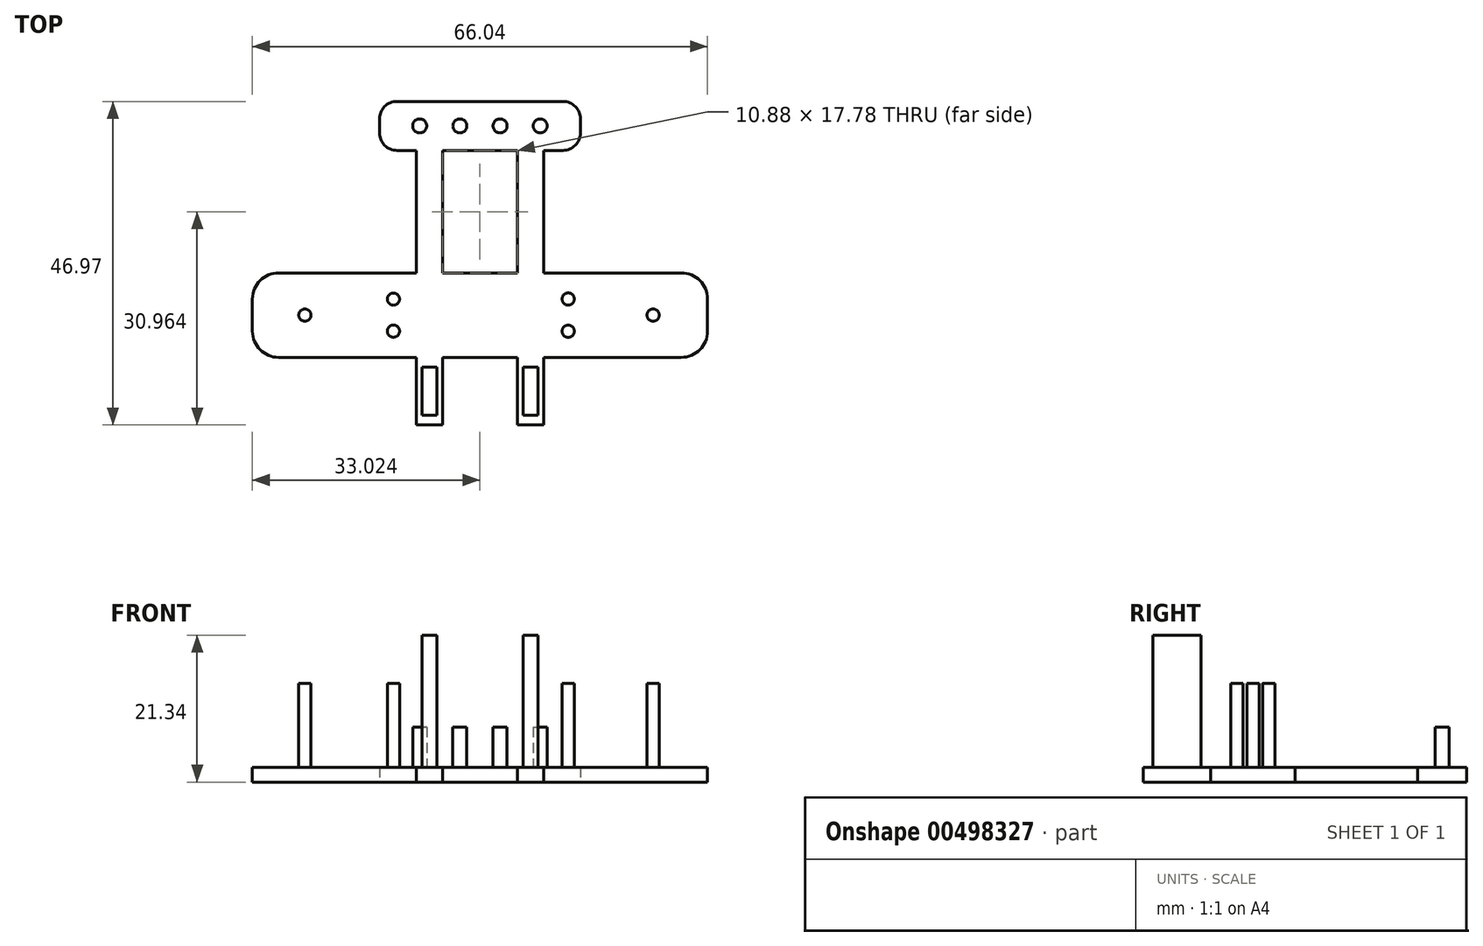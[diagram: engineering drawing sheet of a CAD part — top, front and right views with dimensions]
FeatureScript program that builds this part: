
annotation { "Feature Type Name" : "Feature", "Feature Type Description" : "" }
export const myFeature = defineFeature(function(context is Context, id is Id, definition is map)
    precondition{}
    {
        {
            var Q0;
            Q0=qCreatedBy(makeId("Top.planeOp"),FACE);
            var sketch = newSketch(context, id + "F0", { "sketchPlane" : qUnion([Q0])});
            skLineSegment(sketch, "E0.bottom", {"start": v(33.02, -6.13) * mm, "end": v(-33.02, -6.13) * mm});
            skLineSegment(sketch, "E0.top", {"start": v(29.21, 6.13) * mm, "end": v(-29.21, 6.13) * mm});
            skLineSegment(sketch, "E0.left", {"start": v(33.02, -2.32) * mm, "end": v(33.02, 2.32) * mm});
            skLineSegment(sketch, "E0.right", {"start": v(-33.02, -2.32) * mm, "end": v(-33.02, 2.32) * mm});
            skPoint(sketch, "E0.middle", {"position": v(0, 0) * mm});
            skLineSegment(sketch, "E1", {"start": v(-29.21, -6.13) * mm, "end": v(-9.25, -6.13) * mm});
            skLineSegment(sketch, "E2", {"start": v(29.21, -6.13) * mm, "end": v(9.25, -6.13) * mm});
            skLineSegment(sketch, "E3", {"start": v(9.25, -6.13) * mm, "end": v(9.25, -15.94) * mm});
            skLineSegment(sketch, "E4", {"start": v(9.25, -15.94) * mm, "end": v(5.44, -15.94) * mm});
            skLineSegment(sketch, "E5", {"start": v(5.44, -15.94) * mm, "end": v(5.44, -6.13) * mm});
            skLineSegment(sketch, "E6", {"start": v(-9.25, -6.13) * mm, "end": v(-9.25, -15.94) * mm});
            skLineSegment(sketch, "E7", {"start": v(-9.25, -15.94) * mm, "end": v(-5.44, -15.94) * mm});
            skLineSegment(sketch, "E8", {"start": v(-5.44, -15.94) * mm, "end": v(-5.44, -6.13) * mm});
            skLineSegment(sketch, "E9", {"start": v(-9.25, 6.13) * mm, "end": v(-9.25, 23.91) * mm});
            skLineSegment(sketch, "E10", {"start": v(-9.25, 23.91) * mm, "end": v(-5.44, 23.91) * mm});
            skLineSegment(sketch, "E11", {"start": v(-5.44, 23.91) * mm, "end": v(-5.44, 6.13) * mm});
            skPoint(sketch, "E12.endSnap0", {"position": v(-9.25, 15.02) * mm});
            skLineSegment(sketch, "E13", {"start": v(5.44, 6.13) * mm, "end": v(5.44, 23.91) * mm});
            skLineSegment(sketch, "E14", {"start": v(5.44, 23.91) * mm, "end": v(9.25, 23.91) * mm});
            skLineSegment(sketch, "E15", {"start": v(9.25, 23.91) * mm, "end": v(9.25, 6.13) * mm});
            skPoint(sketch, "E16.startSnap0", {"position": v(0, 6.13) * mm});
            skLineSegment(sketch, "E17", {"start": v(0, 23.91) * mm, "end": v(0, 27.47) * mm});
            skLineSegment(sketch, "E18.bottom", {"start": v(12.04, 23.91) * mm, "end": v(-12.04, 23.91) * mm});
            skLineSegment(sketch, "E18.top", {"start": v(12.04, 31.03) * mm, "end": v(-12.04, 31.03) * mm});
            skLineSegment(sketch, "E18.left", {"start": v(14.58, 26.45) * mm, "end": v(14.58, 28.49) * mm});
            skLineSegment(sketch, "E18.right", {"start": v(-14.58, 26.45) * mm, "end": v(-14.58, 28.49) * mm});
            skPoint(sketch, "E18.middle", {"position": v(0, 27.47) * mm});
            skPoint(sketch, "E19.visualSharp", {"position": v(-33.02, 6.13) * mm});
            skArc(sketch, "E19.filletArc", {"start": v(-29.21, 6.13) * mm, "mid": v(-31.9, 5.02) * mm, "end": v(-33.02, 2.32) * mm});
            skPoint(sketch, "E20.visualSharp", {"position": v(33.02, 6.13) * mm});
            skArc(sketch, "E20.filletArc", {"start": v(33.02, 2.32) * mm, "mid": v(31.9, 5.02) * mm, "end": v(29.21, 6.13) * mm});
            skPoint(sketch, "E21.visualSharp", {"position": v(-14.58, 31.03) * mm});
            skArc(sketch, "E21.filletArc", {"start": v(-12.04, 31.03) * mm, "mid": v(-13.84, 30.28) * mm, "end": v(-14.58, 28.49) * mm});
            skPoint(sketch, "E22.visualSharp", {"position": v(-14.58, 23.91) * mm});
            skArc(sketch, "E22.filletArc", {"start": v(-14.58, 26.45) * mm, "mid": v(-13.84, 24.66) * mm, "end": v(-12.04, 23.91) * mm});
            skPoint(sketch, "E23.visualSharp", {"position": v(14.58, 31.03) * mm});
            skArc(sketch, "E23.filletArc", {"start": v(14.58, 28.49) * mm, "mid": v(13.84, 30.28) * mm, "end": v(12.04, 31.03) * mm});
            skPoint(sketch, "E24.visualSharp", {"position": v(14.58, 23.91) * mm});
            skArc(sketch, "E24.filletArc", {"start": v(12.04, 23.91) * mm, "mid": v(13.84, 24.66) * mm, "end": v(14.58, 26.45) * mm});
            skPoint(sketch, "E25.visualSharp", {"position": v(-33.02, -6.13) * mm});
            skArc(sketch, "E25.filletArc", {"start": v(-33.02, -2.32) * mm, "mid": v(-31.9, -5.02) * mm, "end": v(-29.21, -6.13) * mm});
            skPoint(sketch, "E26.visualSharp", {"position": v(33.02, -6.13) * mm});
            skArc(sketch, "E26.filletArc", {"start": v(29.21, -6.13) * mm, "mid": v(31.9, -5.02) * mm, "end": v(33.02, -2.32) * mm});
            skSolve(sketch);
        }
        {
            var Q0;
            Q0=makeQuery(id+"F0.imprint","IMPRINT",FACE,{"disambiguationData":[TD([[makeQuery(id+"F0.imprint","IMPRINT",EDGE,{"derivedFrom":sQuery(id+"F0.wireOp",EDGE,"E0.left")}),1.0]])]});
            var Q1;
            {var subQ0=sQuery(id+"F0.wireOp",EDGE,"E9");Q1=makeQuery(id+"F0.imprint","IMPRINT",FACE,{"disambiguationData":[TD([[makeQuery(id+"F0.imprint","IMPRINT",EDGE,{"derivedFrom":subQ0}),-1.0]])]});}
            var Q2;
            Q2=makeQuery(id+"F0.imprint","IMPRINT",FACE,{"disambiguationData":[TD([[makeQuery(id+"F0.imprint","IMPRINT",EDGE,{"derivedFrom":sQuery(id+"F0.wireOp",EDGE,"E18.top")}),1.0]])]});
            var Q3;
            {var subQ0=sQuery(id+"F0.wireOp",EDGE,"E13");Q3=makeQuery(id+"F0.imprint","IMPRINT",FACE,{"disambiguationData":[TD([[makeQuery(id+"F0.imprint","IMPRINT",EDGE,{"derivedFrom":subQ0}),-1.0]])]});}
            var Q4;
            {var subQ0=sQuery(id+"F0.wireOp",EDGE,"E3");Q4=makeQuery(id+"F0.imprint","IMPRINT",FACE,{"disambiguationData":[TD([[makeQuery(id+"F0.imprint","IMPRINT",EDGE,{"derivedFrom":subQ0}),-1.0]])]});}
            var Q5;
            {var subQ0=sQuery(id+"F0.wireOp",EDGE,"E6");Q5=makeQuery(id+"F0.imprint","IMPRINT",FACE,{"disambiguationData":[TD([[makeQuery(id+"F0.imprint","IMPRINT",EDGE,{"derivedFrom":subQ0}),1.0]])]});}
            extrude(context, id + "F1", {"entities" : qUnion([Q0, Q1, Q2, Q3, Q4, Q5]), "depth" : 2.16 * mm});
        }
        {
            var Q0;
            Q0=makeQuery(id+"F1.opExtrude","CAP_FACE",FACE,{"disambiguationData":[OSD([sQuery(id+"F0.wireOp",EDGE,"E0.bottom"),sQuery(id+"F0.wireOp",EDGE,"E0.top"),sQuery(id+"F0.wireOp",EDGE,"E0.left"),sQuery(id+"F0.wireOp",EDGE,"E0.right"),sQuery(id+"F0.wireOp",EDGE,"E1"),sQuery(id+"F0.wireOp",EDGE,"E2"),sQuery(id+"F0.wireOp",EDGE,"E3"),sQuery(id+"F0.wireOp",EDGE,"E4"),sQuery(id+"F0.wireOp",EDGE,"E5"),sQuery(id+"F0.wireOp",EDGE,"E6"),sQuery(id+"F0.wireOp",EDGE,"E7"),sQuery(id+"F0.wireOp",EDGE,"E8"),sQuery(id+"F0.wireOp",EDGE,"E9"),sQuery(id+"F0.wireOp",EDGE,"E11"),sQuery(id+"F0.wireOp",EDGE,"E13"),sQuery(id+"F0.wireOp",EDGE,"E15"),sQuery(id+"F0.wireOp",EDGE,"E18.bottom"),sQuery(id+"F0.wireOp",EDGE,"E18.top"),sQuery(id+"F0.wireOp",EDGE,"E18.left"),sQuery(id+"F0.wireOp",EDGE,"E18.right"),sQuery(id+"F0.wireOp",EDGE,"E19.filletArc"),sQuery(id+"F0.wireOp",EDGE,"E20.filletArc"),sQuery(id+"F0.wireOp",EDGE,"E21.filletArc"),sQuery(id+"F0.wireOp",EDGE,"E22.filletArc"),sQuery(id+"F0.wireOp",EDGE,"E23.filletArc"),sQuery(id+"F0.wireOp",EDGE,"E24.filletArc"),sQuery(id+"F0.wireOp",EDGE,"E25.filletArc"),sQuery(id+"F0.wireOp",EDGE,"E26.filletArc")])],"isStart":false});
            var sketch = newSketch(context, id + "F2", { "sketchPlane" : qUnion([Q0])});
            skPoint(sketch, "E27.endSnap0", {"position": v(33.02, 0) * mm});
            skCircle(sketch, "E28", {"center": v(-25.4, 0) * mm, "radius": 0.89 * mm});
            skCircle(sketch, "E29", {"center": v(-12.56, 2.32) * mm, "radius": 0.89 * mm});
            skCircle(sketch, "E30", {"center": v(-12.56, -2.32) * mm, "radius": 0.89 * mm});
            skCircle(sketch, "E31", {"center": v(12.8, -2.34) * mm, "radius": 0.89 * mm});
            skCircle(sketch, "E32", {"center": v(12.8, 2.34) * mm, "radius": 0.89 * mm});
            skCircle(sketch, "E33", {"center": v(25.13, 0) * mm, "radius": 0.89 * mm});
            skSolve(sketch);
        }
        {
            var Q0;
            Q0=makeQuery(id+"F2.imprint","IMPRINT",FACE,{"disambiguationData":[TD([[makeQuery(id+"F2.imprint","IMPRINT",EDGE,{"derivedFrom":sQuery(id+"F2.wireOp",EDGE,"E28")}),1.0]])]});
            var Q1;
            Q1=makeQuery(id+"F2.imprint","IMPRINT",FACE,{"disambiguationData":[TD([[makeQuery(id+"F2.imprint","IMPRINT",EDGE,{"derivedFrom":sQuery(id+"F2.wireOp",EDGE,"E30")}),1.0]])]});
            var Q2;
            Q2=makeQuery(id+"F2.imprint","IMPRINT",FACE,{"disambiguationData":[TD([[makeQuery(id+"F2.imprint","IMPRINT",EDGE,{"derivedFrom":sQuery(id+"F2.wireOp",EDGE,"E29")}),1.0]])]});
            var Q3;
            Q3=makeQuery(id+"F2.imprint","IMPRINT",FACE,{"disambiguationData":[TD([[makeQuery(id+"F2.imprint","IMPRINT",EDGE,{"derivedFrom":sQuery(id+"F2.wireOp",EDGE,"E33")}),1.0]])]});
            var Q4;
            Q4=makeQuery(id+"F2.imprint","IMPRINT",FACE,{"disambiguationData":[TD([[makeQuery(id+"F2.imprint","IMPRINT",EDGE,{"derivedFrom":sQuery(id+"F2.wireOp",EDGE,"E32")}),1.0]])]});
            var Q5;
            Q5=makeQuery(id+"F2.imprint","IMPRINT",FACE,{"disambiguationData":[TD([[makeQuery(id+"F2.imprint","IMPRINT",EDGE,{"derivedFrom":sQuery(id+"F2.wireOp",EDGE,"E31")}),1.0]])]});
            extrude(context, id + "F3", {"entities" : qUnion([Q0, Q1, Q2, Q3, Q4, Q5]), "operationType" : NewBodyOperationType.ADD, "depth" : 12.2 * mm});
        }
        {
            var Q0;
            Q0=makeQuery(id+"F1.opExtrude","CAP_FACE",FACE,{"disambiguationData":[OSD([sQuery(id+"F0.wireOp",EDGE,"E0.bottom"),sQuery(id+"F0.wireOp",EDGE,"E0.top"),sQuery(id+"F0.wireOp",EDGE,"E0.left"),sQuery(id+"F0.wireOp",EDGE,"E0.right"),sQuery(id+"F0.wireOp",EDGE,"E1"),sQuery(id+"F0.wireOp",EDGE,"E2"),sQuery(id+"F0.wireOp",EDGE,"E3"),sQuery(id+"F0.wireOp",EDGE,"E4"),sQuery(id+"F0.wireOp",EDGE,"E5"),sQuery(id+"F0.wireOp",EDGE,"E6"),sQuery(id+"F0.wireOp",EDGE,"E7"),sQuery(id+"F0.wireOp",EDGE,"E8"),sQuery(id+"F0.wireOp",EDGE,"E9"),sQuery(id+"F0.wireOp",EDGE,"E11"),sQuery(id+"F0.wireOp",EDGE,"E13"),sQuery(id+"F0.wireOp",EDGE,"E15"),sQuery(id+"F0.wireOp",EDGE,"E18.bottom"),sQuery(id+"F0.wireOp",EDGE,"E18.top"),sQuery(id+"F0.wireOp",EDGE,"E18.left"),sQuery(id+"F0.wireOp",EDGE,"E18.right"),sQuery(id+"F0.wireOp",EDGE,"E19.filletArc"),sQuery(id+"F0.wireOp",EDGE,"E20.filletArc"),sQuery(id+"F0.wireOp",EDGE,"E21.filletArc"),sQuery(id+"F0.wireOp",EDGE,"E22.filletArc"),sQuery(id+"F0.wireOp",EDGE,"E23.filletArc"),sQuery(id+"F0.wireOp",EDGE,"E24.filletArc"),sQuery(id+"F0.wireOp",EDGE,"E25.filletArc"),sQuery(id+"F0.wireOp",EDGE,"E26.filletArc")])],"isStart":false});
            var sketch = newSketch(context, id + "F4", { "sketchPlane" : qUnion([Q0])});
            skPoint(sketch, "E34.endSnap0", {"position": v(-14.58, 27.47) * mm});
            skCircle(sketch, "E35", {"center": v(-8.75, 27.47) * mm, "radius": 1.02 * mm});
            skCircle(sketch, "E36", {"center": v(-2.92, 27.47) * mm, "radius": 1.02 * mm});
            skCircle(sketch, "E37", {"center": v(2.92, 27.47) * mm, "radius": 1.02 * mm});
            skCircle(sketch, "E38", {"center": v(8.75, 27.47) * mm, "radius": 1.02 * mm});
            skSolve(sketch);
        }
        {
            var Q0;
            Q0=makeQuery(id+"F4.imprint","IMPRINT",FACE,{"disambiguationData":[TD([[makeQuery(id+"F4.imprint","IMPRINT",EDGE,{"derivedFrom":sQuery(id+"F4.wireOp",EDGE,"E35")}),1.0]])]});
            var Q1;
            Q1=makeQuery(id+"F4.imprint","IMPRINT",FACE,{"disambiguationData":[TD([[makeQuery(id+"F4.imprint","IMPRINT",EDGE,{"derivedFrom":sQuery(id+"F4.wireOp",EDGE,"E36")}),1.0]])]});
            var Q2;
            Q2=makeQuery(id+"F4.imprint","IMPRINT",FACE,{"disambiguationData":[TD([[makeQuery(id+"F4.imprint","IMPRINT",EDGE,{"derivedFrom":sQuery(id+"F4.wireOp",EDGE,"E37")}),1.0]])]});
            var Q3;
            Q3=makeQuery(id+"F4.imprint","IMPRINT",FACE,{"disambiguationData":[TD([[makeQuery(id+"F4.imprint","IMPRINT",EDGE,{"derivedFrom":sQuery(id+"F4.wireOp",EDGE,"E38")}),1.0]])]});
            extrude(context, id + "F5", {"entities" : qUnion([Q0, Q1, Q2, Q3]), "operationType" : NewBodyOperationType.ADD, "depth" : 5.84 * mm});
        }
        {
            var Q0;
            Q0=makeQuery(id+"F1.opExtrude","CAP_FACE",FACE,{"disambiguationData":[OSD([sQuery(id+"F0.wireOp",EDGE,"E0.bottom"),sQuery(id+"F0.wireOp",EDGE,"E0.top"),sQuery(id+"F0.wireOp",EDGE,"E0.left"),sQuery(id+"F0.wireOp",EDGE,"E0.right"),sQuery(id+"F0.wireOp",EDGE,"E1"),sQuery(id+"F0.wireOp",EDGE,"E2"),sQuery(id+"F0.wireOp",EDGE,"E3"),sQuery(id+"F0.wireOp",EDGE,"E4"),sQuery(id+"F0.wireOp",EDGE,"E5"),sQuery(id+"F0.wireOp",EDGE,"E6"),sQuery(id+"F0.wireOp",EDGE,"E7"),sQuery(id+"F0.wireOp",EDGE,"E8"),sQuery(id+"F0.wireOp",EDGE,"E9"),sQuery(id+"F0.wireOp",EDGE,"E11"),sQuery(id+"F0.wireOp",EDGE,"E13"),sQuery(id+"F0.wireOp",EDGE,"E15"),sQuery(id+"F0.wireOp",EDGE,"E18.bottom"),sQuery(id+"F0.wireOp",EDGE,"E18.top"),sQuery(id+"F0.wireOp",EDGE,"E18.left"),sQuery(id+"F0.wireOp",EDGE,"E18.right"),sQuery(id+"F0.wireOp",EDGE,"E19.filletArc"),sQuery(id+"F0.wireOp",EDGE,"E20.filletArc"),sQuery(id+"F0.wireOp",EDGE,"E21.filletArc"),sQuery(id+"F0.wireOp",EDGE,"E22.filletArc"),sQuery(id+"F0.wireOp",EDGE,"E23.filletArc"),sQuery(id+"F0.wireOp",EDGE,"E24.filletArc"),sQuery(id+"F0.wireOp",EDGE,"E25.filletArc"),sQuery(id+"F0.wireOp",EDGE,"E26.filletArc")])],"isStart":false});
            var sketch = newSketch(context, id + "F6", { "sketchPlane" : qUnion([Q0])});
            skPoint(sketch, "E39.middle", {"position": v(-7.34, -11.04) * mm});
            skLineSegment(sketch, "E40.bottom", {"start": v(-6.26, -14.52) * mm, "end": v(-8.42, -14.52) * mm});
            skLineSegment(sketch, "E40.top", {"start": v(-6.26, -7.56) * mm, "end": v(-8.42, -7.56) * mm});
            skLineSegment(sketch, "E40.left", {"start": v(-6.26, -14.52) * mm, "end": v(-6.26, -7.56) * mm});
            skLineSegment(sketch, "E40.right", {"start": v(-8.42, -14.52) * mm, "end": v(-8.42, -7.56) * mm});
            skPoint(sketch, "E41.endSnap0", {"position": v(9.25, -11.04) * mm});
            skLineSegment(sketch, "E42.bottom", {"start": v(8.43, -14.52) * mm, "end": v(6.27, -14.52) * mm});
            skLineSegment(sketch, "E42.top", {"start": v(8.43, -7.56) * mm, "end": v(6.27, -7.56) * mm});
            skLineSegment(sketch, "E42.left", {"start": v(8.43, -14.52) * mm, "end": v(8.43, -7.56) * mm});
            skLineSegment(sketch, "E42.right", {"start": v(6.27, -14.52) * mm, "end": v(6.27, -7.56) * mm});
            skPoint(sketch, "E42.middle", {"position": v(7.35, -11.04) * mm});
            skSolve(sketch);
        }
        {
            var Q0;
            Q0 = qSketchRegion(id + "F6", true);
            extrude(context, id + "F7", {"entities" : qUnion([Q0]), "operationType" : NewBodyOperationType.ADD, "depth" : 19.18 * mm});
        }
    });
